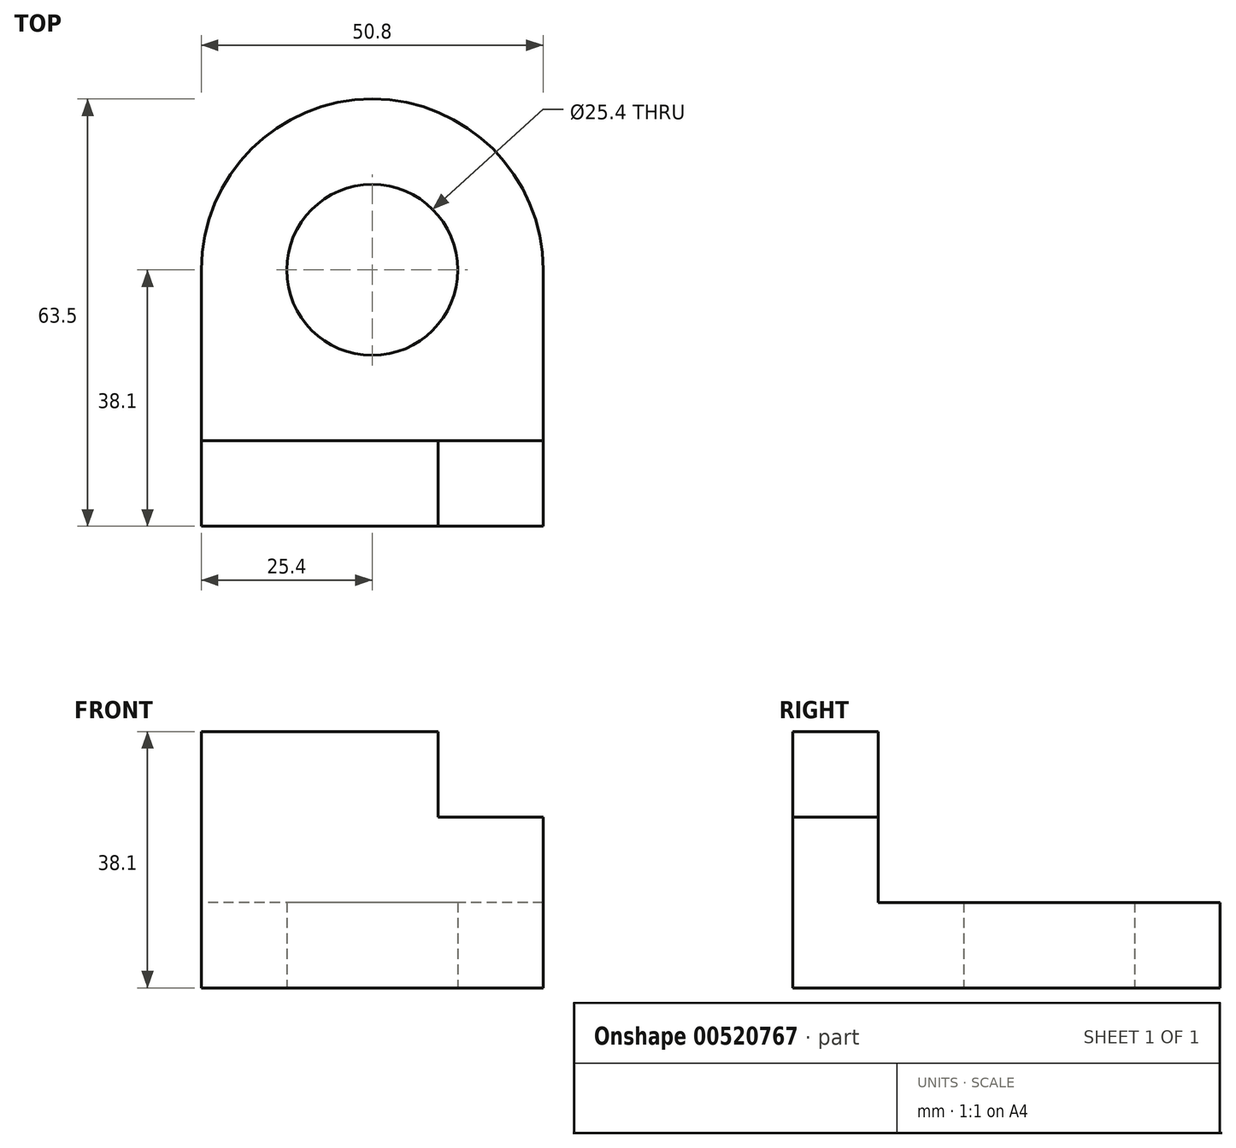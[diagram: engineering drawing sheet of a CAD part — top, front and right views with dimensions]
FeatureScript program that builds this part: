
annotation { "Feature Type Name" : "Feature", "Feature Type Description" : "" }
export const myFeature = defineFeature(function(context is Context, id is Id, definition is map)
    precondition{}
    {
        {
            var Q0;
            Q0=qCreatedBy(makeId("Top.planeOp"),FACE);
            var sketch = newSketch(context, id + "F0", { "sketchPlane" : qUnion([Q0])});
            skCircle(sketch, "E0", {"center": v(0, 0) * mm, "radius": 12.7 * mm});
            skArc(sketch, "E1", {"start": v(25.4, 0) * mm, "mid": v(0, 25.4) * mm, "end": v(-25.4, 0) * mm});
            skLineSegment(sketch, "E2", {"start": v(25.4, 0) * mm, "end": v(25.4, -38.1) * mm});
            skLineSegment(sketch, "E3", {"start": v(25.4, -38.1) * mm, "end": v(-25.4, -38.1) * mm});
            skLineSegment(sketch, "E4", {"start": v(-25.4, -38.1) * mm, "end": v(-25.4, 0) * mm});
            skSolve(sketch);
        }
        {
            var Q0;
            Q0 = qSketchRegion(id + "F0", true);
            extrude(context, id + "F1", {"entities" : qUnion([Q0]), "depth" : 12.7 * mm, "offsetDistance" : 25.4 * mm});
        }
        {
            var Q0;
            Q0=makeQuery(id+"F1.opExtrude","SWEPT_FACE",FACE,{"disambiguationData":[OSD([sQuery(id+"F0.wireOp",EDGE,"E3")])]});
            var sketch = newSketch(context, id + "F2", { "sketchPlane" : qUnion([Q0])});
            skLineSegment(sketch, "E5.bottom", {"start": v(-25.4, 12.7) * mm, "end": v(25.4, 12.7) * mm});
            skLineSegment(sketch, "E5.top", {"start": v(-25.4, 38.1) * mm, "end": v(9.82, 38.1) * mm});
            skLineSegment(sketch, "E5.left", {"start": v(-25.4, 12.7) * mm, "end": v(-25.4, 38.1) * mm});
            skLineSegment(sketch, "E5.right", {"start": v(25.4, 12.7) * mm, "end": v(25.4, 25.4) * mm});
            skLineSegment(sketch, "E6", {"start": v(9.82, 38.1) * mm, "end": v(9.82, 25.4) * mm});
            skPoint(sketch, "E6.endSnap0", {"position": v(25.4, 25.4) * mm});
            skLineSegment(sketch, "E7", {"start": v(9.82, 25.4) * mm, "end": v(25.4, 25.4) * mm});
            skPoint(sketch, "E8.orphan", {"position": v(25.4, 38.1) * mm});
            skSolve(sketch);
        }
        {
            var Q0;
            Q0 = qSketchRegion(id + "F2", true);
            extrude(context, id + "F3", {"entities" : qUnion([Q0]), "operationType" : NewBodyOperationType.ADD, "oppositeDirection" : true, "depth" : 12.7 * mm, "offsetDistance" : 25.4 * mm});
        }
    });
